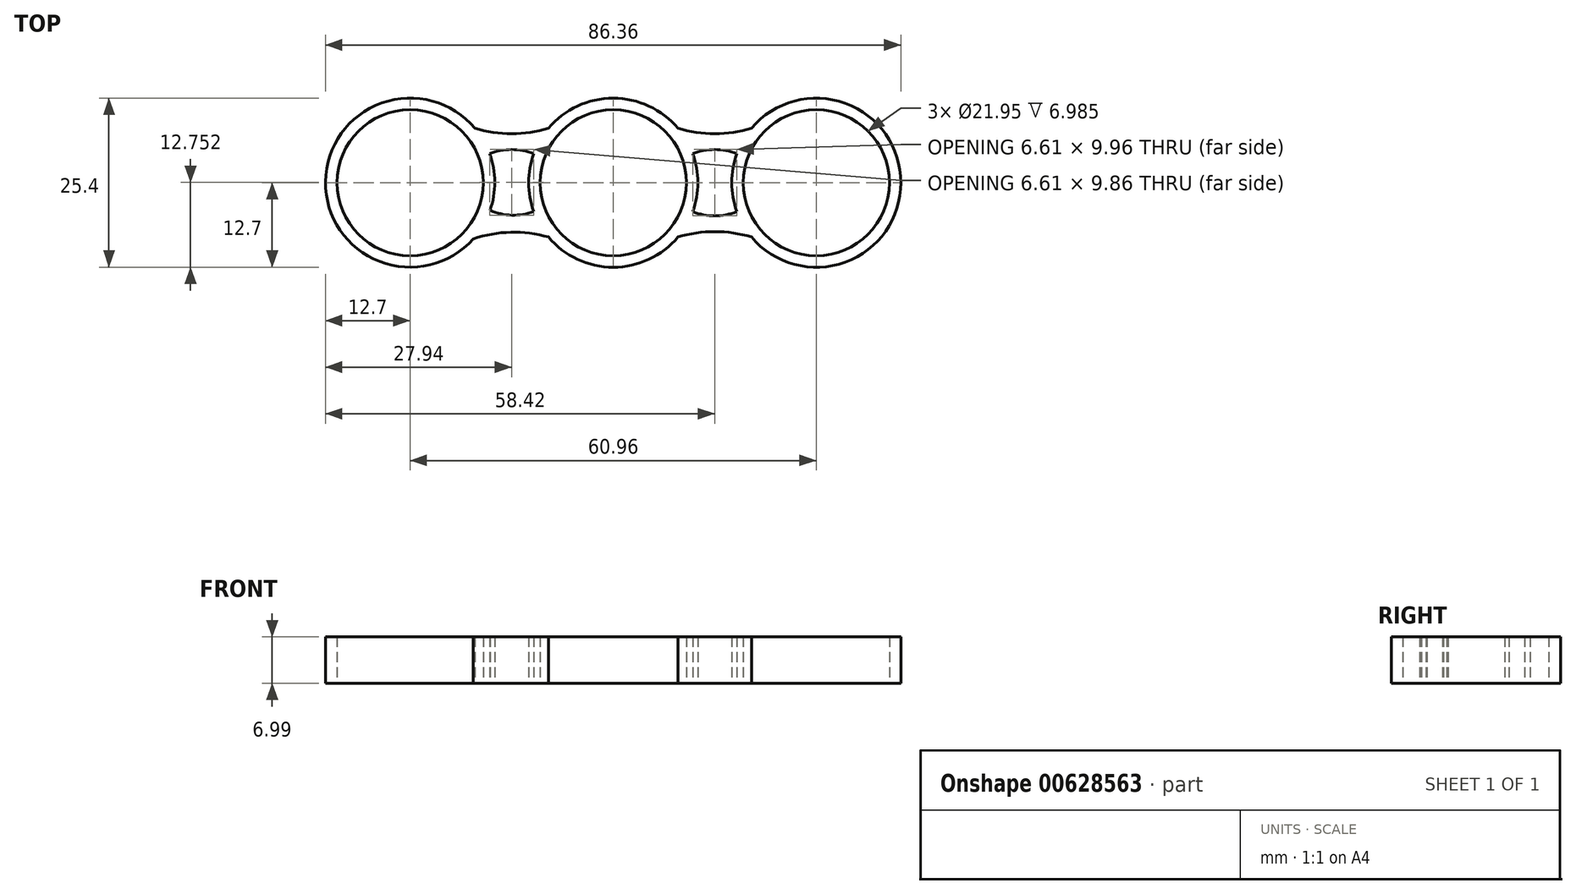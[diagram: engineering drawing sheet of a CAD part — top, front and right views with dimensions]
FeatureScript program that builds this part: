
annotation { "Feature Type Name" : "Feature", "Feature Type Description" : "" }
export const myFeature = defineFeature(function(context is Context, id is Id, definition is map)
    precondition{}
    {
        {
            var Q0;
            Q0=qCreatedBy(makeId("Top.planeOp"),FACE);
            var sketch = newSketch(context, id + "F0", { "sketchPlane" : qUnion([Q0])});
            skCircle(sketch, "E0", {"center": v(0, 0) * mm, "radius": 10.97 * mm});
            skLineSegment(sketch, "E1", {"start": v(0, 0) * mm, "end": v(30.48, 0) * mm});
            skLineSegment(sketch, "E2", {"start": v(0, 0) * mm, "end": v(-30.48, 0) * mm});
            skCircle(sketch, "E3", {"center": v(30.48, 0) * mm, "radius": 10.97 * mm});
            skCircle(sketch, "E4", {"center": v(-30.48, 0) * mm, "radius": 10.97 * mm});
            skLineSegment(sketch, "E5", {"start": v(-30.48, 0) * mm, "end": v(-22.07, 7.05) * mm});
            skLineSegment(sketch, "E6", {"start": v(-30.48, 0) * mm, "end": v(-20.17, 3.75) * mm});
            skLineSegment(sketch, "E7", {"start": v(-30.48, 0) * mm, "end": v(-20.11, -3.6) * mm});
            skLineSegment(sketch, "E8", {"start": v(-30.48, 0) * mm, "end": v(-22.27, -7.28) * mm});
            skLineSegment(sketch, "E9", {"start": v(0, 0) * mm, "end": v(-10.31, 3.75) * mm});
            skLineSegment(sketch, "E10", {"start": v(0, 0) * mm, "end": v(-8.4, 7.05) * mm});
            skLineSegment(sketch, "E11", {"start": v(0, 0) * mm, "end": v(-10.31, -3.75) * mm});
            skLineSegment(sketch, "E12", {"start": v(0, 0) * mm, "end": v(-8.4, -7.05) * mm});
            skLineSegment(sketch, "E13", {"start": v(0, 0) * mm, "end": v(8.4, 7.05) * mm});
            skLineSegment(sketch, "E14", {"start": v(0, 0) * mm, "end": v(10.31, 3.75) * mm});
            skLineSegment(sketch, "E15", {"start": v(0, 0) * mm, "end": v(10.31, -3.75) * mm});
            skLineSegment(sketch, "E16", {"start": v(0, 0) * mm, "end": v(8.4, -7.05) * mm});
            skLineSegment(sketch, "E17", {"start": v(30.48, 0) * mm, "end": v(20.17, 3.75) * mm});
            skLineSegment(sketch, "E18", {"start": v(30.48, 0) * mm, "end": v(22.07, 7.05) * mm});
            skLineSegment(sketch, "E19", {"start": v(30.48, 0) * mm, "end": v(20.17, -3.75) * mm});
            skLineSegment(sketch, "E20", {"start": v(30.48, 0) * mm, "end": v(22.07, -7.05) * mm});
            skCircle(sketch, "E21", {"center": v(-30.48, 0) * mm, "radius": 12.7 * mm});
            skCircle(sketch, "E22", {"center": v(0, 0) * mm, "radius": 12.7 * mm});
            skCircle(sketch, "E23", {"center": v(30.48, 0) * mm, "radius": 12.7 * mm});
            skLineSegment(sketch, "E24", {"start": v(-30.48, 0) * mm, "end": v(-20.98, -8.43) * mm});
            skLineSegment(sketch, "E25", {"start": v(-30.48, 0) * mm, "end": v(-18.48, -4.16) * mm});
            skLineSegment(sketch, "E26", {"start": v(-30.48, 0) * mm, "end": v(-18.55, 4.34) * mm});
            skLineSegment(sketch, "E27", {"start": v(-30.48, 0) * mm, "end": v(-20.75, 8.16) * mm});
            skLineSegment(sketch, "E28", {"start": v(0, 0) * mm, "end": v(-9.73, 8.16) * mm});
            skLineSegment(sketch, "E29", {"start": v(0, 0) * mm, "end": v(-11.93, 4.34) * mm});
            skLineSegment(sketch, "E30", {"start": v(0, 0) * mm, "end": v(-11.93, -4.34) * mm});
            skLineSegment(sketch, "E31", {"start": v(0, 0) * mm, "end": v(-9.73, -8.16) * mm});
            skLineSegment(sketch, "E32", {"start": v(0, 0) * mm, "end": v(9.73, -8.16) * mm});
            skLineSegment(sketch, "E33", {"start": v(0, 0) * mm, "end": v(11.93, -4.34) * mm});
            skLineSegment(sketch, "E34", {"start": v(0, 0) * mm, "end": v(11.93, 4.34) * mm});
            skLineSegment(sketch, "E35", {"start": v(0, 0) * mm, "end": v(9.73, 8.16) * mm});
            skLineSegment(sketch, "E36", {"start": v(30.48, 0) * mm, "end": v(20.75, 8.16) * mm});
            skLineSegment(sketch, "E37", {"start": v(30.48, 0) * mm, "end": v(18.55, 4.34) * mm});
            skLineSegment(sketch, "E38", {"start": v(30.48, 0) * mm, "end": v(18.55, -4.34) * mm});
            skLineSegment(sketch, "E39", {"start": v(30.48, 0) * mm, "end": v(20.75, -8.16) * mm});
            skArc(sketch, "E40", {"start": v(-9.73, -8.16) * mm, "mid": v(-15.38, -7.45) * mm, "end": v(-20.98, -8.43) * mm});
            skArc(sketch, "E41", {"start": v(-18.48, -4.16) * mm, "mid": v(-15.22, -4.88) * mm, "end": v(-11.93, -4.34) * mm});
            skArc(sketch, "E42", {"start": v(-20.75, 8.16) * mm, "mid": v(-15.24, 7.35) * mm, "end": v(-9.73, 8.16) * mm});
            skArc(sketch, "E43", {"start": v(20.75, -8.16) * mm, "mid": v(15.24, -7.35) * mm, "end": v(9.73, -8.16) * mm});
            skArc(sketch, "E44", {"start": v(11.93, -4.34) * mm, "mid": v(15.24, -4.98) * mm, "end": v(18.55, -4.34) * mm});
            skArc(sketch, "E45", {"start": v(9.73, 8.16) * mm, "mid": v(15.24, 7.35) * mm, "end": v(20.75, 8.16) * mm});
            skArc(sketch, "E46", {"start": v(-11.93, 4.34) * mm, "mid": v(-15.24, 4.98) * mm, "end": v(-18.55, 4.34) * mm});
            skArc(sketch, "E47", {"start": v(18.55, 4.34) * mm, "mid": v(15.24, 4.98) * mm, "end": v(11.93, 4.34) * mm});
            skSolve(sketch);
        }
        {
            var Q0;
            Q0 = qSketchRegion(id + "F0", true);
            var Q1;
            {var subQ0=sQuery(id+"F0.wireOp",EDGE,"E21");var subQ1=sQuery(id+"F0.wireOp",EDGE,"E2");var subQ2=makeQuery(id+"F0.imprint","INTERSECT",VERTEX,{"derivedFrom":[subQ1,subQ0]});Q1=makeQuery(id+"F0.imprint","IMPRINT",FACE,{"disambiguationData":[TD([[makeQuery(id+"F0.imprint","IMPRINT",EDGE,{"disambiguationData":[TD([[subQ2,-1.0]])],"derivedFrom":subQ1}),-1.0]])]});}
            var Q2;
            {var subQ0=sQuery(id+"F0.wireOp",EDGE,"E21");var subQ1=sQuery(id+"F0.wireOp",EDGE,"E2");var subQ2=makeQuery(id+"F0.imprint","INTERSECT",VERTEX,{"derivedFrom":[subQ1,subQ0]});Q2=makeQuery(id+"F0.imprint","IMPRINT",FACE,{"disambiguationData":[TD([[makeQuery(id+"F0.imprint","IMPRINT",EDGE,{"disambiguationData":[TD([[subQ2,-1.0]])],"derivedFrom":subQ1}),1.0]])]});}
            var Q3;
            {var subQ0=sQuery(id+"F0.wireOp",EDGE,"E29");var subQ1=sQuery(id+"F0.wireOp",EDGE,"E0");var subQ2=makeQuery(id+"F0.imprint","INTERSECT",VERTEX,{"derivedFrom":[subQ1,subQ0]});Q3=makeQuery(id+"F0.imprint","IMPRINT",FACE,{"disambiguationData":[TD([[makeQuery(id+"F0.imprint","IMPRINT",EDGE,{"disambiguationData":[TD([[subQ2,-1.0]])],"derivedFrom":subQ1}),-1.0]])]});}
            var Q4;
            {var subQ0=sQuery(id+"F0.wireOp",EDGE,"E2");var subQ1=sQuery(id+"F0.wireOp",EDGE,"E0");var subQ2=makeQuery(id+"F0.imprint","INTERSECT",VERTEX,{"derivedFrom":[subQ1,subQ0]});Q4=makeQuery(id+"F0.imprint","IMPRINT",FACE,{"disambiguationData":[TD([[makeQuery(id+"F0.imprint","IMPRINT",EDGE,{"disambiguationData":[TD([[subQ2,-1.0]])],"derivedFrom":subQ1}),-1.0]])]});}
            var Q5;
            {var subQ0=sQuery(id+"F0.wireOp",EDGE,"E34");var subQ1=sQuery(id+"F0.wireOp",EDGE,"E0");var subQ2=makeQuery(id+"F0.imprint","INTERSECT",VERTEX,{"derivedFrom":[subQ1,subQ0]});Q5=makeQuery(id+"F0.imprint","IMPRINT",FACE,{"disambiguationData":[TD([[makeQuery(id+"F0.imprint","IMPRINT",EDGE,{"disambiguationData":[TD([[subQ2,1.0]])],"derivedFrom":subQ1}),-1.0]])]});}
            var Q6;
            {var subQ0=sQuery(id+"F0.wireOp",EDGE,"E1");var subQ1=sQuery(id+"F0.wireOp",EDGE,"E0");var subQ2=makeQuery(id+"F0.imprint","INTERSECT",VERTEX,{"derivedFrom":[subQ1,subQ0]});Q6=makeQuery(id+"F0.imprint","IMPRINT",FACE,{"disambiguationData":[TD([[makeQuery(id+"F0.imprint","IMPRINT",EDGE,{"disambiguationData":[TD([[subQ2,1.0]])],"derivedFrom":subQ1}),-1.0]])]});}
            var Q7;
            {var subQ0=sQuery(id+"F0.wireOp",EDGE,"E23");var subQ1=sQuery(id+"F0.wireOp",EDGE,"E1");var subQ2=makeQuery(id+"F0.imprint","INTERSECT",VERTEX,{"derivedFrom":[subQ1,subQ0]});Q7=makeQuery(id+"F0.imprint","IMPRINT",FACE,{"disambiguationData":[TD([[makeQuery(id+"F0.imprint","IMPRINT",EDGE,{"disambiguationData":[TD([[subQ2,-1.0]])],"derivedFrom":subQ1}),1.0]])]});}
            var Q8;
            {var subQ0=sQuery(id+"F0.wireOp",EDGE,"E23");var subQ1=sQuery(id+"F0.wireOp",EDGE,"E1");var subQ2=makeQuery(id+"F0.imprint","INTERSECT",VERTEX,{"derivedFrom":[subQ1,subQ0]});Q8=makeQuery(id+"F0.imprint","IMPRINT",FACE,{"disambiguationData":[TD([[makeQuery(id+"F0.imprint","IMPRINT",EDGE,{"disambiguationData":[TD([[subQ2,-1.0]])],"derivedFrom":subQ1}),-1.0]])]});}
            extrude(context, id + "F1", {"entities" : qUnion([Q0, Q1, Q2, Q3, Q4, Q5, Q6, Q7, Q8]), "depth" : 7 * mm, "offsetDistance" : 25.4 * mm});
        }
    });
